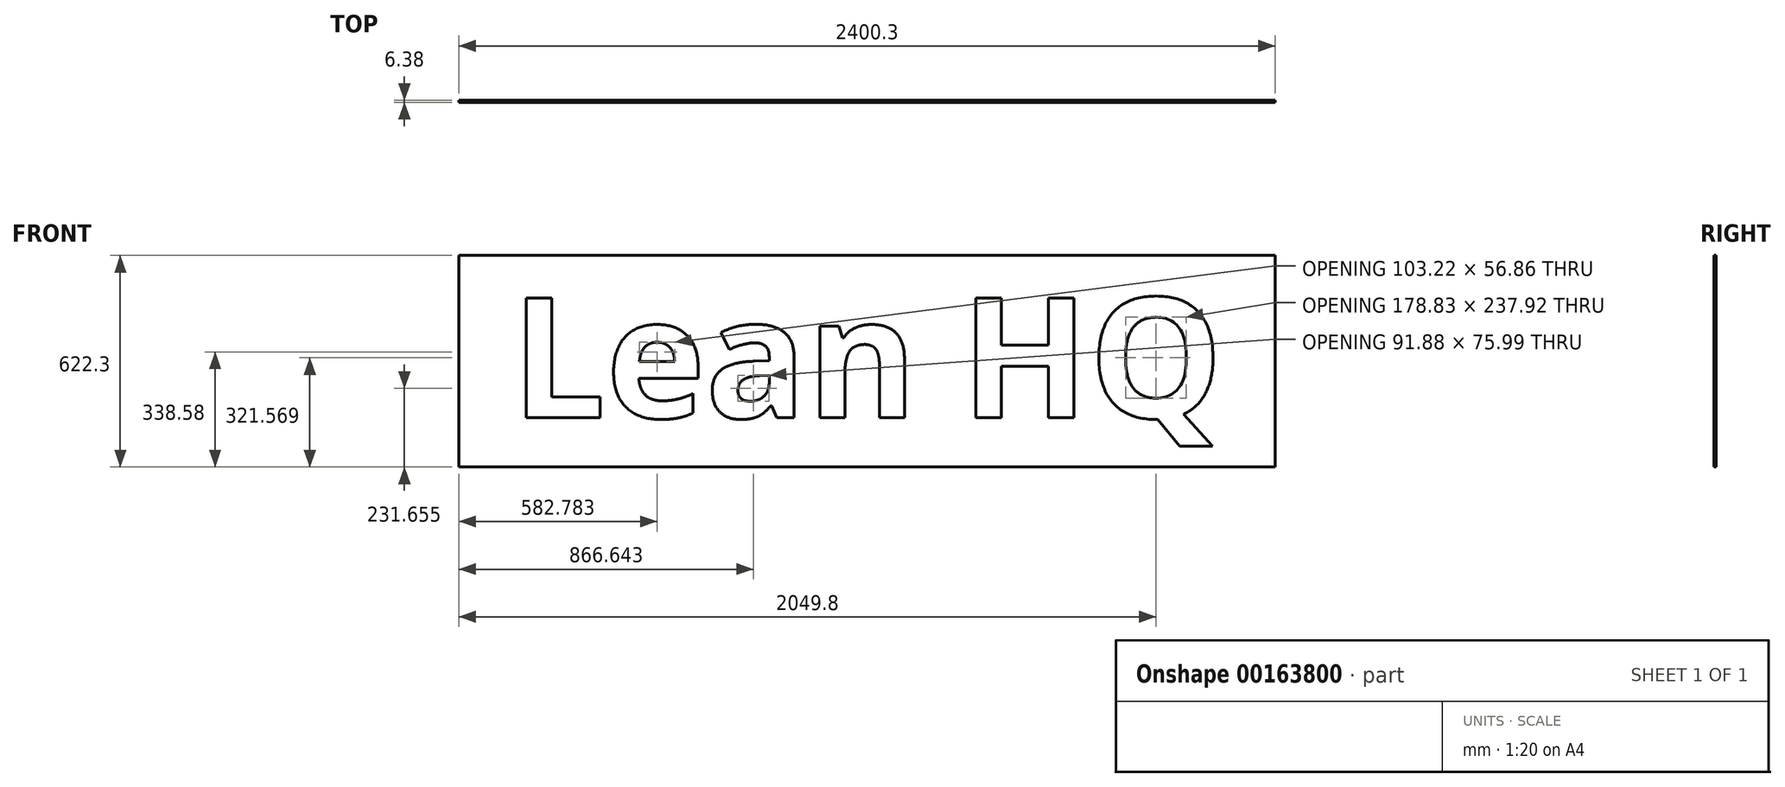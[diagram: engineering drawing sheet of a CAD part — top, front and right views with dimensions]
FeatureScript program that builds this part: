
annotation { "Feature Type Name" : "Feature", "Feature Type Description" : "" }
export const myFeature = defineFeature(function(context is Context, id is Id, definition is map)
    precondition{}
    {
        {
            var Q0;
            Q0=qCreatedBy(makeId("Front.planeOp"),FACE);
            var sketch = newSketch(context, id + "F0", { "sketchPlane" : qUnion([Q0])});
            skLineSegment(sketch, "E0.bottom", {"start": v(-1200.15, -311.15) * mm, "end": v(1200.15, -311.15) * mm});
            skLineSegment(sketch, "E0.top", {"start": v(-1200.15, 311.15) * mm, "end": v(1200.15, 311.15) * mm});
            skLineSegment(sketch, "E0.left", {"start": v(-1200.15, -311.15) * mm, "end": v(-1200.15, 311.15) * mm});
            skLineSegment(sketch, "E0.right", {"start": v(1200.15, -311.15) * mm, "end": v(1200.15, 311.15) * mm});
            skPoint(sketch, "E0.middle", {"position": v(0, 0) * mm});
            skSolve(sketch);
        }
        {
            var Q0;
            Q0=makeQuery(id+"F0.imprint","IMPRINT",FACE,{"disambiguationData":[TD([[makeQuery(id+"F0.imprint","IMPRINT",EDGE,{"derivedFrom":sQuery(id+"F0.wireOp",EDGE,"8d6b9380-7f4e-47b4-9038-9769c137446f.sketch_text.stroke-93")}),1.0]])]});
            var Q1;
            Q1=makeQuery(id+"F0.imprint","IMPRINT",FACE,{"disambiguationData":[TD([[makeQuery(id+"F0.imprint","IMPRINT",EDGE,{"derivedFrom":sQuery(id+"F0.wireOp",EDGE,"8d6b9380-7f4e-47b4-9038-9769c137446f.sketch_text.stroke-44")}),1.0]])]});
            var Q2;
            Q2=makeQuery(id+"F0.imprint","IMPRINT",FACE,{"disambiguationData":[TD([[makeQuery(id+"F0.imprint","IMPRINT",EDGE,{"derivedFrom":sQuery(id+"F0.wireOp",EDGE,"8d6b9380-7f4e-47b4-9038-9769c137446f.sketch_text.stroke-20")}),1.0]])]});
            var Q3;
            Q3=makeQuery(id+"F0.imprint","IMPRINT",FACE,{"disambiguationData":[TD([[makeQuery(id+"F0.imprint","IMPRINT",EDGE,{"derivedFrom":sQuery(id+"F0.wireOp",EDGE,"E0.bottom")}),1.0]])]});
            extrude(context, id + "F1", {"entities" : qUnion([Q0, Q1, Q2, Q3]), "depth" : 6.35 * mm});
        }
        {
            var Q0;
            Q0=makeQuery(id+"F1.opExtrude","CAP_FACE",FACE,{"disambiguationData":[OSD([sQuery(id+"F0.wireOp",EDGE,"E0.bottom"),sQuery(id+"F0.wireOp",EDGE,"E0.top"),sQuery(id+"F0.wireOp",EDGE,"E0.left"),sQuery(id+"F0.wireOp",EDGE,"E0.right")])],"isStart":false});
            var sketch = newSketch(context, id + "F2", { "sketchPlane" : qUnion([Q0])});
            skText(sketch, "E1", { "text": "Lean HQ", "fontName": "OpenSans-Bold.ttf"});
            const initialGuessF2  = {"E1": [-1.0463, -0.1664, 1, 0, 0.35549]};
            skSetInitialGuess(sketch, initialGuessF2);
            skSolve(sketch);
        }
        {
            var Q0;
            Q0 = qSketchRegion(id + "F2", true);
            extrude(context, id + "F3", {"entities" : qUnion([Q0]), "depth" : 0.03 * mm});
        }
    });
